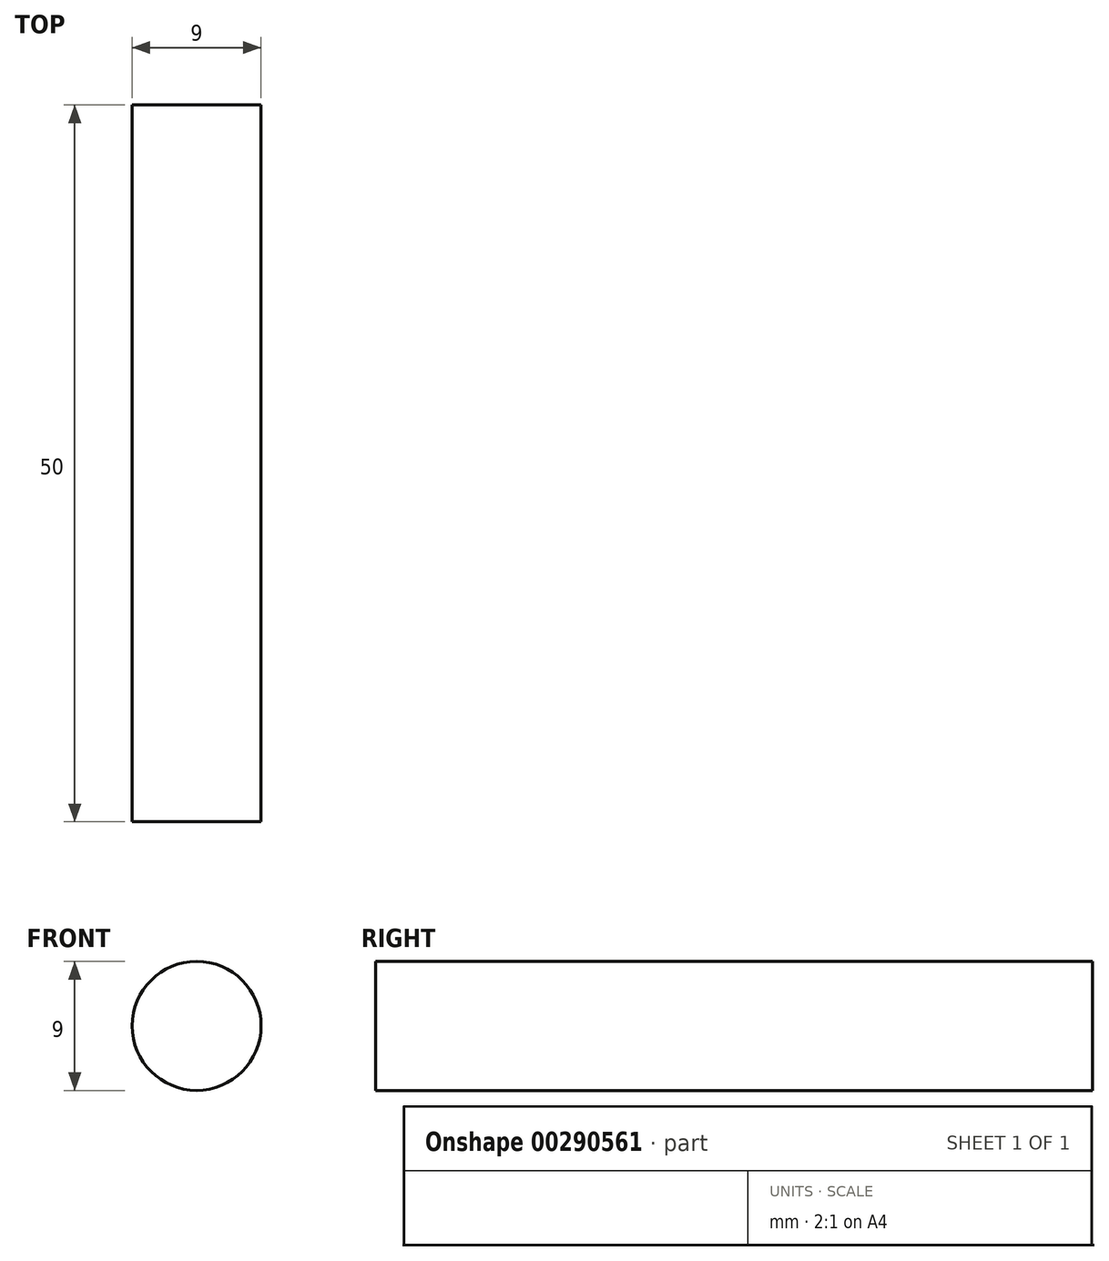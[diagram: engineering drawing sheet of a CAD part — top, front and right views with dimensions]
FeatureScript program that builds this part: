
annotation { "Feature Type Name" : "Feature", "Feature Type Description" : "" }
export const myFeature = defineFeature(function(context is Context, id is Id, definition is map)
    precondition{}
    {
        {
            var Q0;
            Q0=qCreatedBy(makeId("Front.planeOp"),FACE);
            var sketch = newSketch(context, id + "F0", { "sketchPlane" : qUnion([Q0])});
            skCircle(sketch, "E0", {"center": v(0, 0) * mm, "radius": 4.5 * mm});
            skSolve(sketch);
        }
        {
            var Q0;
            Q0 = qSketchRegion(id + "F0", true);
            extrude(context, id + "F1", {"entities" : qUnion([Q0]), "depth" : 50 * mm});
        }
    });
